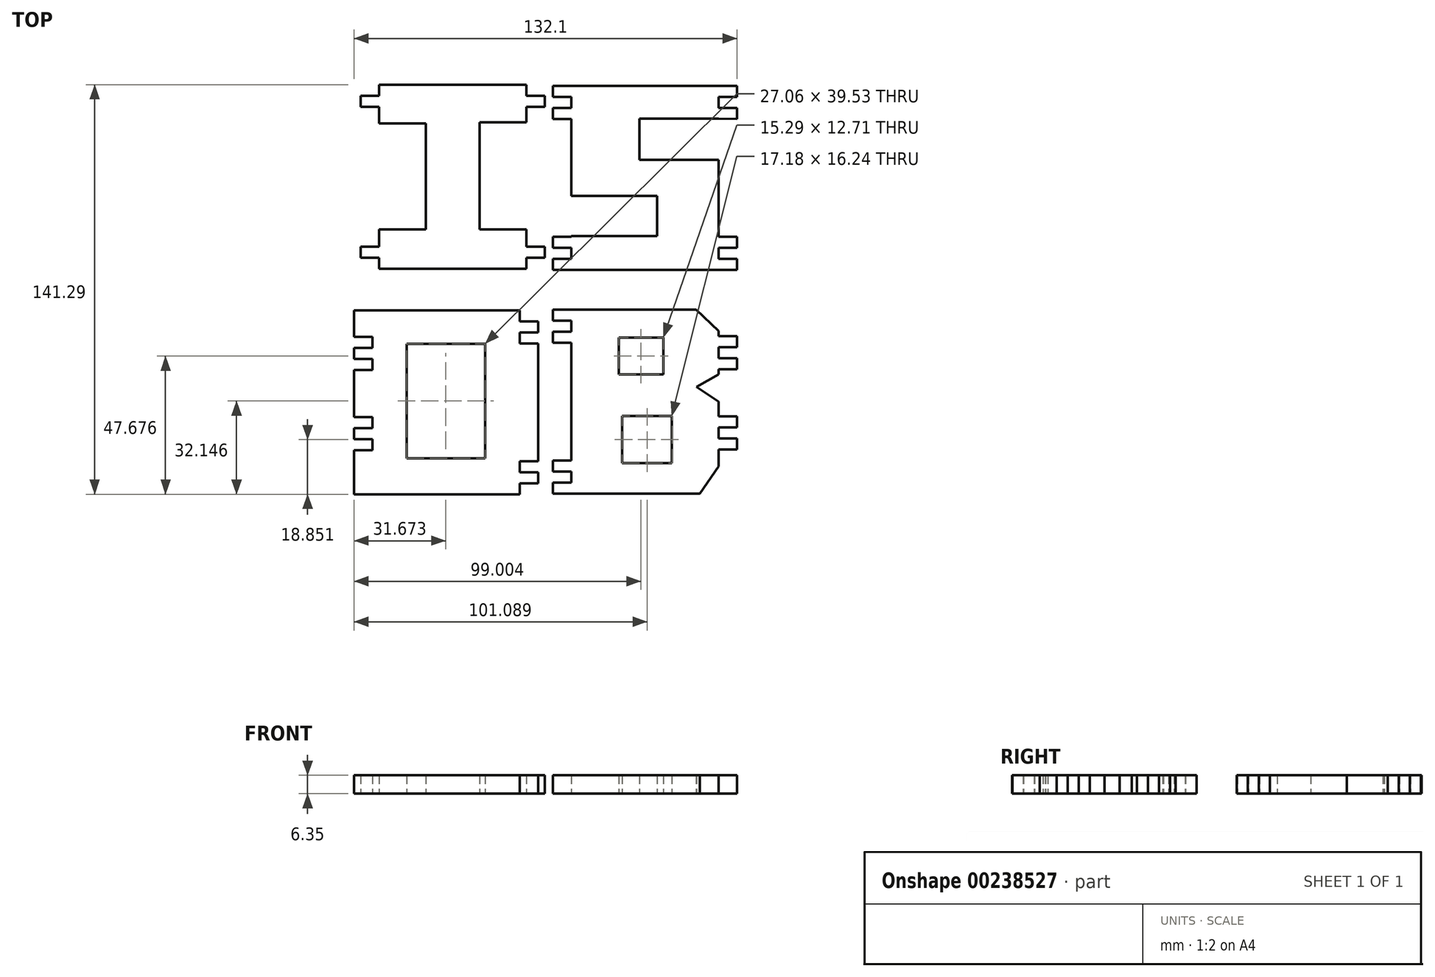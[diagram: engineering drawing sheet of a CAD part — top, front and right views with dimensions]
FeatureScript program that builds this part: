
annotation { "Feature Type Name" : "Feature", "Feature Type Description" : "" }
export const myFeature = defineFeature(function(context is Context, id is Id, definition is map)
    precondition{}
    {
        {
            var Q0;
            Q0=qCreatedBy(makeId("Top.planeOp"),FACE);
            var sketch = newSketch(context, id + "F0", { "sketchPlane" : qUnion([Q0])});
            skLineSegment(sketch, "E0.bottom", {"start": v(6.35, 71.77) * mm, "end": v(57.15, 71.77) * mm});
            skLineSegment(sketch, "E0.top", {"start": v(6.35, 8.27) * mm, "end": v(57.15, 8.27) * mm});
            skLineSegment(sketch, "E0.left", {"start": v(6.35, 71.77) * mm, "end": v(6.35, 8.27) * mm});
            skLineSegment(sketch, "E0.right", {"start": v(57.15, 71.77) * mm, "end": v(57.15, 8.27) * mm});
            skLineSegment(sketch, "E1.bottom", {"start": v(57.15, 60.35) * mm, "end": v(29.81, 60.35) * mm});
            skLineSegment(sketch, "E1.top", {"start": v(57.15, 46.23) * mm, "end": v(29.81, 46.23) * mm});
            skLineSegment(sketch, "E1.left", {"start": v(57.15, 60.35) * mm, "end": v(57.15, 46.23) * mm});
            skLineSegment(sketch, "E1.right", {"start": v(29.81, 60.35) * mm, "end": v(29.81, 46.23) * mm});
            skLineSegment(sketch, "E2.bottom", {"start": v(6.35, 33.76) * mm, "end": v(35.93, 33.76) * mm});
            skLineSegment(sketch, "E2.top", {"start": v(6.35, 19.88) * mm, "end": v(35.93, 19.88) * mm});
            skLineSegment(sketch, "E2.left", {"start": v(6.35, 33.76) * mm, "end": v(6.35, 19.88) * mm});
            skLineSegment(sketch, "E2.right", {"start": v(35.93, 33.76) * mm, "end": v(35.93, 19.88) * mm});
            skLineSegment(sketch, "E3", {"start": v(6.35, 71.77) * mm, "end": v(0, 71.77) * mm});
            skLineSegment(sketch, "E4", {"start": v(0, 71.77) * mm, "end": v(0, 67.96) * mm});
            skLineSegment(sketch, "E5", {"start": v(0, 67.96) * mm, "end": v(6.35, 67.96) * mm});
            skLineSegment(sketch, "E6", {"start": v(6.35, 64.15) * mm, "end": v(0, 64.15) * mm});
            skLineSegment(sketch, "E7", {"start": v(0, 64.15) * mm, "end": v(0, 60.34) * mm});
            skLineSegment(sketch, "E8", {"start": v(0, 60.34) * mm, "end": v(6.35, 60.34) * mm});
            skLineSegment(sketch, "E9", {"start": v(6.35, 8.27) * mm, "end": v(0, 8.27) * mm});
            skLineSegment(sketch, "E10", {"start": v(0, 8.27) * mm, "end": v(0, 12.08) * mm});
            skLineSegment(sketch, "E11", {"start": v(0, 12.08) * mm, "end": v(6.35, 12.08) * mm});
            skLineSegment(sketch, "E12", {"start": v(6.35, 15.89) * mm, "end": v(0, 15.89) * mm});
            skLineSegment(sketch, "E13", {"start": v(0, 15.89) * mm, "end": v(0, 19.7) * mm});
            skLineSegment(sketch, "E14", {"start": v(0, 19.7) * mm, "end": v(6.35, 19.7) * mm});
            skLineSegment(sketch, "E15", {"start": v(57.15, 71.77) * mm, "end": v(63.5, 71.77) * mm});
            skLineSegment(sketch, "E16", {"start": v(63.5, 71.77) * mm, "end": v(63.5, 67.96) * mm});
            skLineSegment(sketch, "E17", {"start": v(63.5, 67.96) * mm, "end": v(57.15, 67.96) * mm});
            skLineSegment(sketch, "E18", {"start": v(57.15, 64.15) * mm, "end": v(63.5, 64.15) * mm});
            skLineSegment(sketch, "E19", {"start": v(63.5, 64.15) * mm, "end": v(63.5, 60.34) * mm});
            skLineSegment(sketch, "E20", {"start": v(63.5, 60.34) * mm, "end": v(57.15, 60.35) * mm});
            skLineSegment(sketch, "E21", {"start": v(57.15, 8.27) * mm, "end": v(63.5, 8.27) * mm});
            skLineSegment(sketch, "E22", {"start": v(63.5, 8.27) * mm, "end": v(63.5, 12.08) * mm});
            skLineSegment(sketch, "E23", {"start": v(63.5, 12.08) * mm, "end": v(57.15, 12.08) * mm});
            skLineSegment(sketch, "E24", {"start": v(57.15, 19.7) * mm, "end": v(63.5, 19.7) * mm});
            skLineSegment(sketch, "E25", {"start": v(63.5, 19.7) * mm, "end": v(63.5, 15.89) * mm});
            skLineSegment(sketch, "E26", {"start": v(63.5, 15.89) * mm, "end": v(57.15, 15.89) * mm});
            skSolve(sketch);
        }
        {
            var Q0;
            Q0=qCreatedBy(makeId("Top.planeOp"),FACE);
            var sketch = newSketch(context, id + "F1", { "sketchPlane" : qUnion([Q0])});
            skLineSegment(sketch, "E27.bottom", {"start": v(-66.32, 72.08) * mm, "end": v(-2.82, 72.08) * mm});
            skLineSegment(sketch, "E27.top", {"start": v(-66.32, 8.58) * mm, "end": v(-2.82, 8.58) * mm});
            skLineSegment(sketch, "E27.left", {"start": v(-66.32, 72.08) * mm, "end": v(-66.32, 8.58) * mm});
            skLineSegment(sketch, "E27.right", {"start": v(-2.82, 72.08) * mm, "end": v(-2.82, 8.58) * mm});
            skLineSegment(sketch, "E28.bottom", {"start": v(-66.32, 58.7) * mm, "end": v(-43.88, 58.7) * mm});
            skLineSegment(sketch, "E28.top", {"start": v(-66.32, 22.23) * mm, "end": v(-43.88, 22.23) * mm});
            skLineSegment(sketch, "E28.left", {"start": v(-66.32, 58.7) * mm, "end": v(-66.32, 22.23) * mm});
            skLineSegment(sketch, "E28.right", {"start": v(-43.88, 58.7) * mm, "end": v(-43.88, 22.23) * mm});
            skLineSegment(sketch, "E29.bottom", {"start": v(-2.82, 59.18) * mm, "end": v(-25.25, 59.18) * mm});
            skLineSegment(sketch, "E29.top", {"start": v(-2.82, 22.23) * mm, "end": v(-25.25, 22.23) * mm});
            skLineSegment(sketch, "E29.left", {"start": v(-2.82, 59.18) * mm, "end": v(-2.82, 22.23) * mm});
            skLineSegment(sketch, "E29.right", {"start": v(-25.25, 59.18) * mm, "end": v(-25.25, 22.23) * mm});
            skLineSegment(sketch, "E30", {"start": v(-9.17, 72.08) * mm, "end": v(-9.17, 68.27) * mm});
            skLineSegment(sketch, "E31", {"start": v(-9.17, 68.27) * mm, "end": v(-2.82, 68.27) * mm});
            skLineSegment(sketch, "E32", {"start": v(-2.82, 64.46) * mm, "end": v(-9.17, 64.46) * mm});
            skLineSegment(sketch, "E33", {"start": v(-9.17, 64.46) * mm, "end": v(-9.17, 60.65) * mm});
            skLineSegment(sketch, "E34", {"start": v(-9.17, 60.65) * mm, "end": v(-2.82, 60.65) * mm});
            skLineSegment(sketch, "E35", {"start": v(-9.17, 8.58) * mm, "end": v(-9.17, 12.39) * mm});
            skLineSegment(sketch, "E36", {"start": v(-9.17, 12.39) * mm, "end": v(-2.82, 12.39) * mm});
            skLineSegment(sketch, "E37", {"start": v(-2.82, 20) * mm, "end": v(-9.17, 20) * mm});
            skLineSegment(sketch, "E38", {"start": v(-9.17, 20) * mm, "end": v(-9.17, 16.2) * mm});
            skLineSegment(sketch, "E39", {"start": v(-9.17, 16.2) * mm, "end": v(-2.82, 16.2) * mm});
            skLineSegment(sketch, "E40", {"start": v(-59.97, 72.08) * mm, "end": v(-59.97, 64.46) * mm});
            skLineSegment(sketch, "E41", {"start": v(-59.97, 64.46) * mm, "end": v(-66.32, 64.46) * mm});
            skLineSegment(sketch, "E42", {"start": v(-66.32, 68.27) * mm, "end": v(-59.97, 68.27) * mm});
            skLineSegment(sketch, "E43", {"start": v(-59.97, 68.27) * mm, "end": v(-59.97, 60.65) * mm});
            skLineSegment(sketch, "E44", {"start": v(-59.97, 60.65) * mm, "end": v(-66.32, 60.65) * mm});
            skLineSegment(sketch, "E45", {"start": v(-59.97, 8.58) * mm, "end": v(-59.97, 12.39) * mm});
            skLineSegment(sketch, "E46", {"start": v(-59.97, 12.39) * mm, "end": v(-66.32, 12.39) * mm});
            skLineSegment(sketch, "E47", {"start": v(-66.32, 20) * mm, "end": v(-59.97, 20) * mm});
            skLineSegment(sketch, "E48", {"start": v(-59.97, 20) * mm, "end": v(-59.97, 16.2) * mm});
            skLineSegment(sketch, "E49", {"start": v(-59.97, 16.2) * mm, "end": v(-66.32, 16.2) * mm});
            skLineSegment(sketch, "E50", {"start": v(-59.97, 60.65) * mm, "end": v(-59.97, 58.7) * mm});
            skLineSegment(sketch, "E51", {"start": v(-9.17, 60.65) * mm, "end": v(-9.17, 59.18) * mm});
            skLineSegment(sketch, "E52", {"start": v(-59.97, 20) * mm, "end": v(-59.97, 22.23) * mm});
            skLineSegment(sketch, "E53", {"start": v(-9.17, 20) * mm, "end": v(-9.17, 22.23) * mm});
            skSolve(sketch);
        }
        {
            var Q0;
            Q0=qCreatedBy(makeId("Top.planeOp"),FACE);
            var sketch = newSketch(context, id + "F2", { "sketchPlane" : qUnion([Q0])});
            skLineSegment(sketch, "E54.bottom", {"start": v(-68.6, -5.71) * mm, "end": v(-5.1, -5.71) * mm});
            skLineSegment(sketch, "E54.top", {"start": v(-68.6, -69.21) * mm, "end": v(-5.1, -69.21) * mm});
            skLineSegment(sketch, "E54.left", {"start": v(-68.6, -5.71) * mm, "end": v(-68.6, -69.21) * mm});
            skLineSegment(sketch, "E54.right", {"start": v(-5.1, -5.71) * mm, "end": v(-5.1, -69.21) * mm});
            skLineSegment(sketch, "E55.bottom", {"start": v(-50.46, -17.3) * mm, "end": v(-23.4, -17.3) * mm});
            skLineSegment(sketch, "E55.top", {"start": v(-50.46, -56.83) * mm, "end": v(-23.4, -56.83) * mm});
            skLineSegment(sketch, "E55.left", {"start": v(-50.46, -17.3) * mm, "end": v(-50.46, -56.83) * mm});
            skLineSegment(sketch, "E55.right", {"start": v(-23.4, -17.3) * mm, "end": v(-23.4, -56.83) * mm});
            skLineSegment(sketch, "E56", {"start": v(-68.6, -14.86) * mm, "end": v(-62.25, -14.86) * mm});
            skLineSegment(sketch, "E57", {"start": v(-62.25, -14.86) * mm, "end": v(-62.25, -18.67) * mm});
            skLineSegment(sketch, "E58", {"start": v(-62.25, -18.67) * mm, "end": v(-68.6, -18.67) * mm});
            skLineSegment(sketch, "E59", {"start": v(-68.6, -22.48) * mm, "end": v(-62.25, -22.48) * mm});
            skLineSegment(sketch, "E60", {"start": v(-62.25, -22.48) * mm, "end": v(-62.25, -26.29) * mm});
            skLineSegment(sketch, "E61", {"start": v(-62.25, -26.29) * mm, "end": v(-68.6, -26.29) * mm});
            skLineSegment(sketch, "E62", {"start": v(-68.6, -50.16) * mm, "end": v(-62.25, -50.16) * mm});
            skLineSegment(sketch, "E63", {"start": v(-62.25, -53.97) * mm, "end": v(-62.25, -50.16) * mm});
            skLineSegment(sketch, "E64", {"start": v(-62.25, -53.97) * mm, "end": v(-68.6, -53.97) * mm});
            skLineSegment(sketch, "E65", {"start": v(-68.6, -46.35) * mm, "end": v(-62.25, -46.35) * mm});
            skLineSegment(sketch, "E66", {"start": v(-62.25, -46.35) * mm, "end": v(-62.25, -42.54) * mm});
            skLineSegment(sketch, "E67", {"start": v(-62.25, -42.54) * mm, "end": v(-68.6, -42.54) * mm});
            skLineSegment(sketch, "E68", {"start": v(-11.45, -5.71) * mm, "end": v(-11.45, -9.52) * mm});
            skLineSegment(sketch, "E69", {"start": v(-11.45, -9.52) * mm, "end": v(-5.1, -9.52) * mm});
            skLineSegment(sketch, "E70", {"start": v(-5.1, -13.33) * mm, "end": v(-11.45, -13.33) * mm});
            skLineSegment(sketch, "E71", {"start": v(-11.45, -13.33) * mm, "end": v(-11.45, -17.14) * mm});
            skLineSegment(sketch, "E72", {"start": v(-11.45, -17.14) * mm, "end": v(-5.1, -17.14) * mm});
            skLineSegment(sketch, "E73", {"start": v(-11.45, -69.21) * mm, "end": v(-11.45, -65.4) * mm});
            skLineSegment(sketch, "E74", {"start": v(-11.45, -65.4) * mm, "end": v(-5.1, -65.4) * mm});
            skLineSegment(sketch, "E75", {"start": v(-5.1, -57.78) * mm, "end": v(-11.45, -57.78) * mm});
            skLineSegment(sketch, "E76", {"start": v(-11.45, -57.78) * mm, "end": v(-11.45, -61.6) * mm});
            skLineSegment(sketch, "E77", {"start": v(-11.45, -61.6) * mm, "end": v(-5.1, -61.6) * mm});
            skSolve(sketch);
        }
        {
            var Q0;
            Q0=qCreatedBy(makeId("Top.planeOp"),FACE);
            var sketch = newSketch(context, id + "F3", { "sketchPlane" : qUnion([Q0])});
            skLineSegment(sketch, "E78.bottom", {"start": v(6.35, -5.5) * mm, "end": v(57.15, -5.5) * mm});
            skLineSegment(sketch, "E78.top", {"start": v(6.35, -69) * mm, "end": v(57.15, -69) * mm});
            skLineSegment(sketch, "E78.left", {"start": v(6.35, -5.5) * mm, "end": v(6.35, -69) * mm});
            skLineSegment(sketch, "E78.right", {"start": v(57.15, -5.5) * mm, "end": v(57.15, -69) * mm});
            skLineSegment(sketch, "E79.bottom", {"start": v(22.76, -15.18) * mm, "end": v(38.05, -15.18) * mm});
            skLineSegment(sketch, "E79.top", {"start": v(22.76, -27.89) * mm, "end": v(38.05, -27.89) * mm});
            skLineSegment(sketch, "E79.left", {"start": v(22.76, -15.18) * mm, "end": v(22.76, -27.89) * mm});
            skLineSegment(sketch, "E79.right", {"start": v(38.05, -15.18) * mm, "end": v(38.05, -27.89) * mm});
            skLineSegment(sketch, "E80.bottom", {"start": v(23.9, -42.24) * mm, "end": v(41.08, -42.24) * mm});
            skLineSegment(sketch, "E80.top", {"start": v(23.9, -58.48) * mm, "end": v(41.08, -58.48) * mm});
            skLineSegment(sketch, "E80.left", {"start": v(23.9, -42.24) * mm, "end": v(23.9, -58.48) * mm});
            skLineSegment(sketch, "E80.right", {"start": v(41.08, -42.24) * mm, "end": v(41.08, -58.48) * mm});
            skLineSegment(sketch, "E81", {"start": v(49.58, -32.12) * mm, "end": v(57.15, -27.89) * mm});
            skLineSegment(sketch, "E82", {"start": v(49.58, -32.12) * mm, "end": v(57.15, -37.25) * mm});
            skLineSegment(sketch, "E83", {"start": v(49.35, -5.5) * mm, "end": v(57.15, -12.83) * mm});
            skLineSegment(sketch, "E84", {"start": v(57.15, -59.65) * mm, "end": v(50.72, -69) * mm});
            skLineSegment(sketch, "E85", {"start": v(6.35, -5.5) * mm, "end": v(0, -5.5) * mm});
            skLineSegment(sketch, "E86", {"start": v(0, -5.5) * mm, "end": v(0, -9.3) * mm});
            skLineSegment(sketch, "E87", {"start": v(0, -9.3) * mm, "end": v(6.35, -9.3) * mm});
            skLineSegment(sketch, "E88", {"start": v(6.35, -13.12) * mm, "end": v(0, -13.12) * mm});
            skLineSegment(sketch, "E89", {"start": v(0, -13.12) * mm, "end": v(0, -16.93) * mm});
            skLineSegment(sketch, "E90", {"start": v(0, -16.93) * mm, "end": v(6.35, -16.93) * mm});
            skLineSegment(sketch, "E91", {"start": v(6.35, -69) * mm, "end": v(0, -69) * mm});
            skLineSegment(sketch, "E92", {"start": v(0, -69) * mm, "end": v(0, -65.19) * mm});
            skLineSegment(sketch, "E93", {"start": v(0, -65.19) * mm, "end": v(6.35, -65.19) * mm});
            skLineSegment(sketch, "E94", {"start": v(6.35, -57.57) * mm, "end": v(0, -57.57) * mm});
            skLineSegment(sketch, "E95", {"start": v(0, -57.57) * mm, "end": v(0, -61.38) * mm});
            skLineSegment(sketch, "E96", {"start": v(0, -61.38) * mm, "end": v(6.35, -61.38) * mm});
            skLineSegment(sketch, "E97", {"start": v(57.15, -14.64) * mm, "end": v(63.5, -14.64) * mm});
            skLineSegment(sketch, "E98", {"start": v(63.5, -14.64) * mm, "end": v(63.5, -18.45) * mm});
            skLineSegment(sketch, "E99", {"start": v(63.5, -18.45) * mm, "end": v(57.15, -18.45) * mm});
            skLineSegment(sketch, "E100", {"start": v(57.15, -22.26) * mm, "end": v(63.5, -22.26) * mm});
            skLineSegment(sketch, "E101", {"start": v(63.5, -22.26) * mm, "end": v(63.5, -26.07) * mm});
            skLineSegment(sketch, "E102", {"start": v(63.5, -26.07) * mm, "end": v(57.15, -26.07) * mm});
            skLineSegment(sketch, "E103", {"start": v(57.15, -42.33) * mm, "end": v(63.5, -42.33) * mm});
            skLineSegment(sketch, "E104", {"start": v(63.5, -42.33) * mm, "end": v(63.5, -46.14) * mm});
            skLineSegment(sketch, "E105", {"start": v(63.5, -46.14) * mm, "end": v(57.15, -46.14) * mm});
            skLineSegment(sketch, "E106", {"start": v(57.15, -49.95) * mm, "end": v(63.5, -49.95) * mm});
            skLineSegment(sketch, "E107", {"start": v(63.5, -49.95) * mm, "end": v(63.5, -53.76) * mm});
            skLineSegment(sketch, "E108", {"start": v(63.5, -53.76) * mm, "end": v(57.15, -53.76) * mm});
            skSolve(sketch);
        }
        {
            var Q0;
            {var subQ1=sQuery(id+"F0.wireOp",EDGE,"E0.bottom");Q0=makeQuery(id+"F0.imprint","IMPRINT",FACE,{"disambiguationData":[TD([[makeQuery(id+"F0.imprint","IMPRINT",EDGE,{"derivedFrom":subQ1}),-1.0]])]});}
            var Q1;
            {var subQ0=sQuery(id+"F0.wireOp",EDGE,"E3");Q1=makeQuery(id+"F0.imprint","IMPRINT",FACE,{"disambiguationData":[TD([[makeQuery(id+"F0.imprint","IMPRINT",EDGE,{"derivedFrom":subQ0}),1.0]])]});}
            var Q2;
            {var subQ0=sQuery(id+"F0.wireOp",EDGE,"E6");Q2=makeQuery(id+"F0.imprint","IMPRINT",FACE,{"disambiguationData":[TD([[makeQuery(id+"F0.imprint","IMPRINT",EDGE,{"derivedFrom":subQ0}),1.0]])]});}
            var Q3;
            {var subQ0=sQuery(id+"F0.wireOp",EDGE,"E12");Q3=makeQuery(id+"F0.imprint","IMPRINT",FACE,{"disambiguationData":[TD([[makeQuery(id+"F0.imprint","IMPRINT",EDGE,{"derivedFrom":subQ0}),-1.0]])]});}
            var Q4;
            {var subQ0=sQuery(id+"F0.wireOp",EDGE,"E9");Q4=makeQuery(id+"F0.imprint","IMPRINT",FACE,{"disambiguationData":[TD([[makeQuery(id+"F0.imprint","IMPRINT",EDGE,{"derivedFrom":subQ0}),-1.0]])]});}
            var Q5;
            {var subQ0=sQuery(id+"F0.wireOp",EDGE,"E15");Q5=makeQuery(id+"F0.imprint","IMPRINT",FACE,{"disambiguationData":[TD([[makeQuery(id+"F0.imprint","IMPRINT",EDGE,{"derivedFrom":subQ0}),-1.0]])]});}
            var Q6;
            {var subQ2=sQuery(id+"F0.wireOp",EDGE,"E18");Q6=makeQuery(id+"F0.imprint","IMPRINT",FACE,{"disambiguationData":[TD([[makeQuery(id+"F0.imprint","IMPRINT",EDGE,{"derivedFrom":subQ2}),-1.0]])]});}
            var Q7;
            {var subQ0=sQuery(id+"F0.wireOp",EDGE,"E24");Q7=makeQuery(id+"F0.imprint","IMPRINT",FACE,{"disambiguationData":[TD([[makeQuery(id+"F0.imprint","IMPRINT",EDGE,{"derivedFrom":subQ0}),-1.0]])]});}
            var Q8;
            {var subQ0=sQuery(id+"F0.wireOp",EDGE,"E21");Q8=makeQuery(id+"F0.imprint","IMPRINT",FACE,{"disambiguationData":[TD([[makeQuery(id+"F0.imprint","IMPRINT",EDGE,{"derivedFrom":subQ0}),1.0]])]});}
            extrude(context, id + "F4", {"entities" : qUnion([Q0, Q1, Q2, Q3, Q4, Q5, Q6, Q7, Q8]), "depth" : 6.35 * mm});
        }
        {
            var Q0;
            {var subQ4=sQuery(id+"F3.wireOp",EDGE,"E78.left");Q0=makeQuery(id+"F3.imprint","IMPRINT",FACE,{"disambiguationData":[TD([[makeQuery(id+"F3.imprint","IMPRINT",EDGE,{"derivedFrom":subQ4}),1.0]])]});}
            var Q1;
            {var subQ0=sQuery(id+"F3.wireOp",EDGE,"E85");Q1=makeQuery(id+"F3.imprint","IMPRINT",FACE,{"disambiguationData":[TD([[makeQuery(id+"F3.imprint","IMPRINT",EDGE,{"derivedFrom":subQ0}),1.0]])]});}
            var Q2;
            {var subQ0=sQuery(id+"F3.wireOp",EDGE,"E88");Q2=makeQuery(id+"F3.imprint","IMPRINT",FACE,{"disambiguationData":[TD([[makeQuery(id+"F3.imprint","IMPRINT",EDGE,{"derivedFrom":subQ0}),1.0]])]});}
            var Q3;
            {var subQ0=sQuery(id+"F3.wireOp",EDGE,"E94");Q3=makeQuery(id+"F3.imprint","IMPRINT",FACE,{"disambiguationData":[TD([[makeQuery(id+"F3.imprint","IMPRINT",EDGE,{"derivedFrom":subQ0}),1.0]])]});}
            var Q4;
            {var subQ0=sQuery(id+"F3.wireOp",EDGE,"E91");Q4=makeQuery(id+"F3.imprint","IMPRINT",FACE,{"disambiguationData":[TD([[makeQuery(id+"F3.imprint","IMPRINT",EDGE,{"derivedFrom":subQ0}),-1.0]])]});}
            var Q5;
            {var subQ0=sQuery(id+"F3.wireOp",EDGE,"E97");Q5=makeQuery(id+"F3.imprint","IMPRINT",FACE,{"disambiguationData":[TD([[makeQuery(id+"F3.imprint","IMPRINT",EDGE,{"derivedFrom":subQ0}),-1.0]])]});}
            var Q6;
            {var subQ0=sQuery(id+"F3.wireOp",EDGE,"E100");Q6=makeQuery(id+"F3.imprint","IMPRINT",FACE,{"disambiguationData":[TD([[makeQuery(id+"F3.imprint","IMPRINT",EDGE,{"derivedFrom":subQ0}),-1.0]])]});}
            var Q7;
            {var subQ0=sQuery(id+"F3.wireOp",EDGE,"E103");Q7=makeQuery(id+"F3.imprint","IMPRINT",FACE,{"disambiguationData":[TD([[makeQuery(id+"F3.imprint","IMPRINT",EDGE,{"derivedFrom":subQ0}),-1.0]])]});}
            var Q8;
            {var subQ0=sQuery(id+"F3.wireOp",EDGE,"E106");Q8=makeQuery(id+"F3.imprint","IMPRINT",FACE,{"disambiguationData":[TD([[makeQuery(id+"F3.imprint","IMPRINT",EDGE,{"derivedFrom":subQ0}),-1.0]])]});}
            extrude(context, id + "F5", {"entities" : qUnion([Q0, Q1, Q2, Q3, Q4, Q5, Q6, Q7, Q8]), "depth" : 6.35 * mm});
        }
        {
            var Q0;
            Q0=makeQuery(id+"F1.imprint","IMPRINT",FACE,{"disambiguationData":[TD([[makeQuery(id+"F1.imprint","IMPRINT",EDGE,{"derivedFrom":sQuery(id+"F1.wireOp",EDGE,"kcw3VA4t-zObg-aJuu-d5Zn-37pDePq4eIvW")}),1.0]])]});
            var Q1;
            {var subQ0=sQuery(id+"F1.wireOp",EDGE,"qCwyAvs0-fDXk-nOzf-SruF-eOpKyvjlildg");Q1=makeQuery(id+"F1.imprint","IMPRINT",FACE,{"disambiguationData":[TD([[makeQuery(id+"F1.imprint","IMPRINT",EDGE,{"derivedFrom":subQ0}),1.0]])]});}
            var Q2;
            {var subQ0=sQuery(id+"F1.wireOp",EDGE,"E41");Q2=makeQuery(id+"F1.imprint","IMPRINT",FACE,{"disambiguationData":[TD([[makeQuery(id+"F1.imprint","IMPRINT",EDGE,{"derivedFrom":subQ0}),-1.0]])]});}
            var Q3;
            {var subQ14=sQuery(id+"F1.wireOp",EDGE,"E28.right");Q3=makeQuery(id+"F1.imprint","IMPRINT",FACE,{"disambiguationData":[TD([[makeQuery(id+"F1.imprint","IMPRINT",EDGE,{"derivedFrom":subQ14}),1.0]])]});}
            extrude(context, id + "F6", {"entities" : qUnion([Q0, Q1, Q2, Q3]), "depth" : 6.35 * mm});
        }
        {
            var Q0;
            Q0=makeQuery(id+"F2.imprint","IMPRINT",FACE,{"disambiguationData":[TD([[makeQuery(id+"F2.imprint","IMPRINT",EDGE,{"derivedFrom":sQuery(id+"F2.wireOp",EDGE,"E55.bottom")}),1.0]])]});
            extrude(context, id + "F7", {"entities" : qUnion([Q0]), "depth" : 6.35 * mm});
        }
    });
